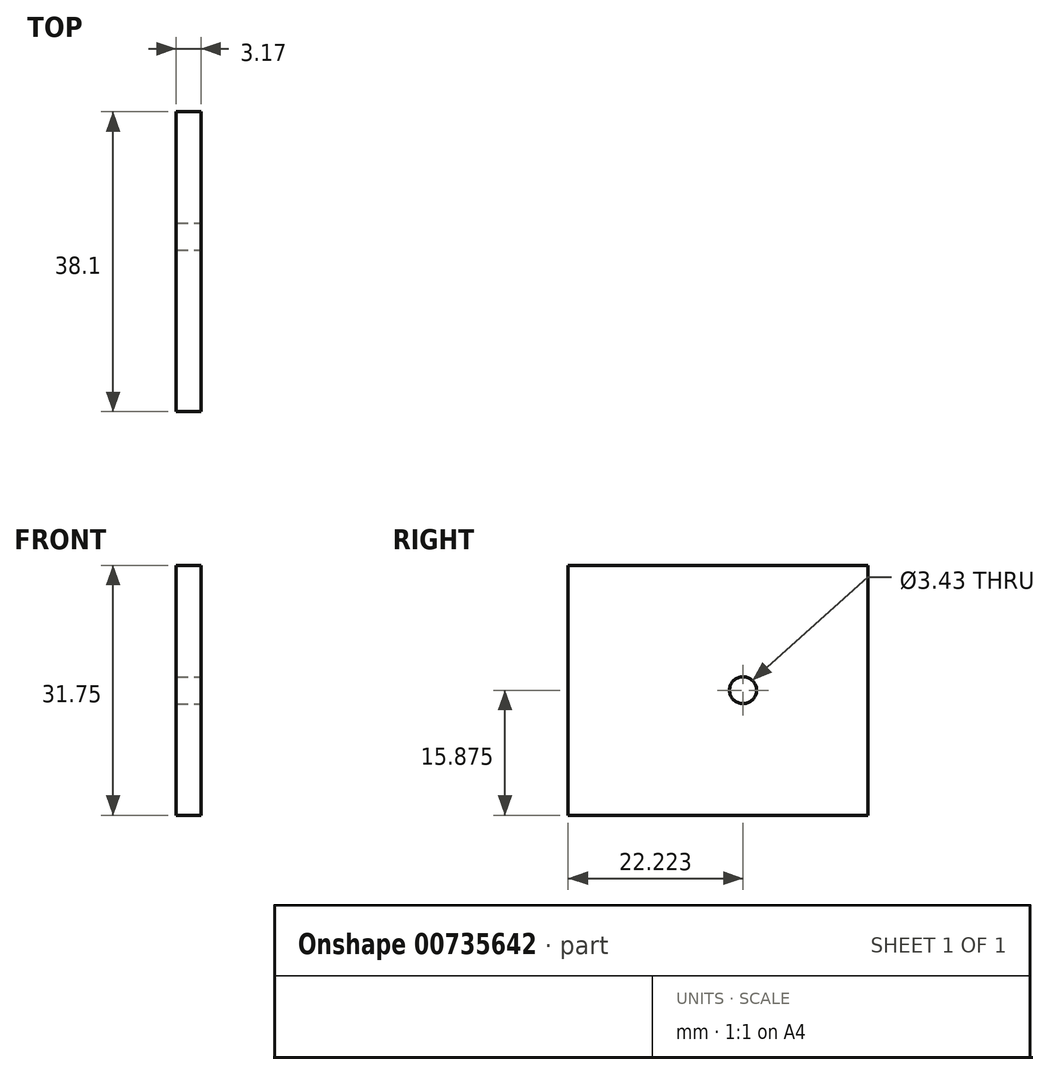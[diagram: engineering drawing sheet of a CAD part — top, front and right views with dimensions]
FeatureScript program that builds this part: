
annotation { "Feature Type Name" : "Feature", "Feature Type Description" : "" }
export const myFeature = defineFeature(function(context is Context, id is Id, definition is map)
    precondition{}
    {
        {
            var Q0;
            Q0=qCreatedBy(makeId("Top.planeOp"),FACE);
            var sketch = newSketch(context, id + "F0", { "sketchPlane" : qUnion([Q0])});
            skLineSegment(sketch, "E0.bottom", {"start": v(-50.78, -11.1) * mm, "end": v(-47.6, -11.1) * mm});
            skLineSegment(sketch, "E0.top", {"start": v(-50.78, -49.2) * mm, "end": v(-47.6, -49.2) * mm});
            skLineSegment(sketch, "E0.left", {"start": v(-50.78, -11.1) * mm, "end": v(-50.78, -49.2) * mm});
            skLineSegment(sketch, "E0.right", {"start": v(-47.6, -11.1) * mm, "end": v(-47.6, -49.2) * mm});
            skSolve(sketch);
        }
        {
            var Q0;
            Q0 = qSketchRegion(id + "F0", true);
            extrude(context, id + "F1", {"entities" : qUnion([Q0]), "depth" : 31.75 * mm, "offsetDistance" : 25.4 * mm});
        }
        {
            var Q0;
            Q0=makeQuery(id+"F1.opExtrude","SWEPT_FACE",FACE,{"disambiguationData":[OSD([sQuery(id+"F0.wireOp",EDGE,"E0.right")])]});
            var sketch = newSketch(context, id + "F2", { "sketchPlane" : qUnion([Q0])});
            skCircle(sketch, "E1", {"center": v(-26.97, 15.88) * mm, "radius": 1.71 * mm});
            skSolve(sketch);
        }
        {
            var Q0;
            Q0=makeQuery(id+"F2.imprint","IMPRINT",FACE,{"disambiguationData":[TD([[makeQuery(id+"F2.imprint","IMPRINT",EDGE,{"derivedFrom":sQuery(id+"F2.wireOp",EDGE,"E1")}),1.0]])]});
            var Q1;
            Q1=sQuery(id+"F2.wireOp",EDGE,"E1");
            extrude(context, id + "F3", {"entities" : qUnion([Q0]), "operationType" : NewBodyOperationType.REMOVE, "surfaceEntities" : qUnion([Q1]), "endBound" : BoundingType.THROUGH_ALL, "oppositeDirection" : true, "depth" : 3.17 * mm, "offsetDistance" : 25.4 * mm});
        }
    });
